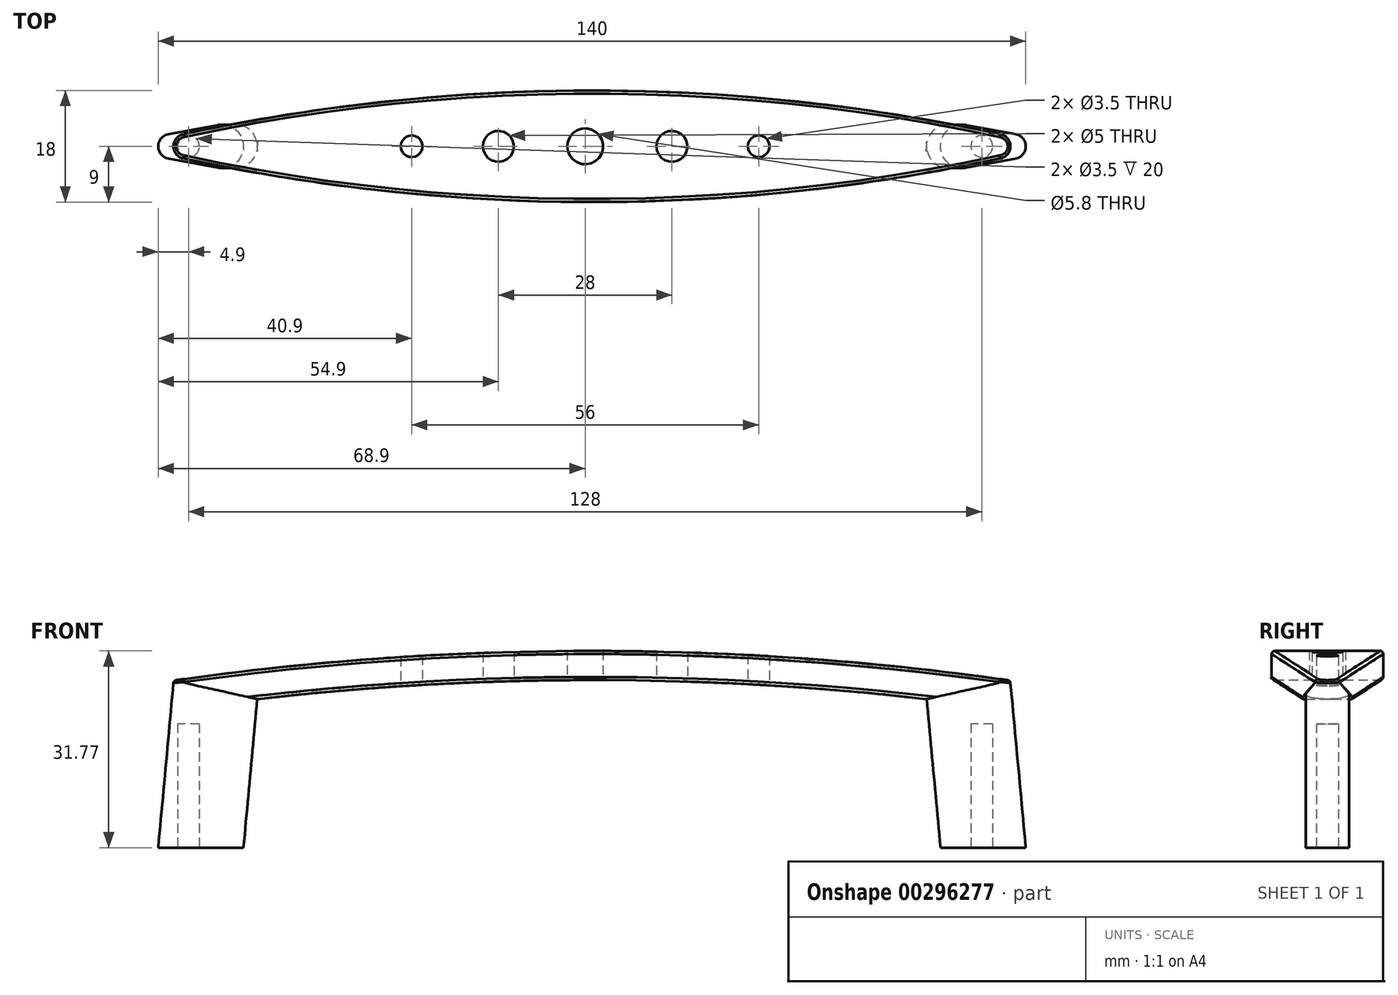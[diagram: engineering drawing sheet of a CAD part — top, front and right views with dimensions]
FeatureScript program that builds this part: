
annotation { "Feature Type Name" : "Feature", "Feature Type Description" : "" }
export const myFeature = defineFeature(function(context is Context, id is Id, definition is map)
    precondition{}
    {
        {
            var Q0;
            Q0=qCreatedBy(makeId("Front.planeOp"),FACE);
            var sketch = newSketch(context, id + "F0", { "sketchPlane" : qUnion([Q0])});
            skLineSegment(sketch, "E0", {"start": v(-66.42, 27) * mm, "end": v(68.58, 27) * mm, "construction": true});
            skLineSegment(sketch, "E1", {"start": v(-66.42, 27) * mm, "end": v(-68.9, 0) * mm});
            skLineSegment(sketch, "E2", {"start": v(68.58, 27) * mm, "end": v(71.1, 0) * mm});
            skLineSegment(sketch, "E3.0", {"start": v(-52.93, 24) * mm, "end": v(-55.14, 0) * mm});
            skLineSegment(sketch, "E4.0", {"start": v(55.1, 24) * mm, "end": v(57.34, 0) * mm});
            skLineSegment(sketch, "E5.0", {"start": v(-52.93, 24) * mm, "end": v(55.1, 24) * mm, "construction": true});
            skLineSegment(sketch, "E6", {"start": v(-68.9, 0) * mm, "end": v(-55.14, 0) * mm});
            skLineSegment(sketch, "E7", {"start": v(71.1, 0) * mm, "end": v(57.34, 0) * mm});
            skArc(sketch, "E8", {"start": v(68.58, 27) * mm, "mid": v(1.08, 31.77) * mm, "end": v(-66.42, 27) * mm});
            skArc(sketch, "E9", {"start": v(55.1, 24) * mm, "mid": v(1.09, 27.07) * mm, "end": v(-52.93, 24) * mm});
            skLineSegment(sketch, "E10", {"start": v(55.1, 24) * mm, "end": v(68.58, 27) * mm});
            skLineSegment(sketch, "E11", {"start": v(-52.93, 24) * mm, "end": v(-66.42, 27) * mm});
            skSolve(sketch);
        }
        {
            var Q0;
            Q0=qCreatedBy(makeId("Top.planeOp"),FACE);
            cPlane(context, id + "F1", {"entities" : qUnion([Q0]), "cplaneType" : CPlaneType.OFFSET, "offset" : 27 * mm, "width" : 150 * mm, "height" : 150 * mm});
        }
        {
            var Q0;
            Q0=qCreatedBy(id+"F1.planeOp",FACE);
            var sketch = newSketch(context, id + "F2", { "sketchPlane" : qUnion([Q0])});
            skCircle(sketch, "E12", {"center": v(66.58, 0) * mm, "radius": 2 * mm});
            skCircle(sketch, "E13", {"center": v(-64.42, 0) * mm, "radius": 2 * mm});
            skArc(sketch, "E14", {"start": v(-64.84, -1.95) * mm, "mid": v(1.08, -9) * mm, "end": v(67, -1.95) * mm});
            skArc(sketch, "E15", {"start": v(67, 1.95) * mm, "mid": v(1.08, 9) * mm, "end": v(-64.84, 1.95) * mm});
            skSolve(sketch);
        }
        {
            var Q0;
            Q0=qCreatedBy(makeId("Top.planeOp"),FACE);
            var sketch = newSketch(context, id + "F3", { "sketchPlane" : qUnion([Q0])});
            skArc(sketch, "E16", {"start": v(61.48, 3.44) * mm, "mid": v(57.34, 0) * mm, "end": v(61.48, -3.44) * mm});
            skArc(sketch, "E17", {"start": v(-59.27, -3.44) * mm, "mid": v(-55.14, 0) * mm, "end": v(-59.27, 3.44) * mm});
            skArc(sketch, "E18", {"start": v(69.47, -1.97) * mm, "mid": v(71.1, 0) * mm, "end": v(69.47, 1.97) * mm});
            skArc(sketch, "E19", {"start": v(-67.26, 1.97) * mm, "mid": v(-68.9, 0) * mm, "end": v(-67.26, -1.97) * mm});
            skLineSegment(sketch, "E20", {"start": v(69.47, -1.97) * mm, "end": v(61.48, -3.44) * mm});
            skLineSegment(sketch, "E21", {"start": v(69.47, 1.97) * mm, "end": v(61.48, 3.44) * mm});
            skLineSegment(sketch, "E22", {"start": v(-59.27, 3.44) * mm, "end": v(-67.26, 1.97) * mm});
            skLineSegment(sketch, "E23", {"start": v(-59.27, -3.44) * mm, "end": v(-67.26, -1.97) * mm});
            skSolve(sketch);
        }
        {
            var Q0;
            Q0=makeQuery(id+"F3.imprint","IMPRINT",FACE,{"disambiguationData":[TD([[makeQuery(id+"F3.imprint","IMPRINT",EDGE,{"derivedFrom":sQuery(id+"F3.wireOp",EDGE,"E16")}),1.0]])]});
            var Q1;
            Q1=sQuery(id+"F0.wireOp",EDGE,"E2");
            sweep(context, id + "F4", {"profiles" : qUnion([Q0]), "path" : qUnion([Q1])});
        }
        {
            var Q0;
            Q0=makeQuery(id+"F3.imprint","IMPRINT",FACE,{"disambiguationData":[TD([[makeQuery(id+"F3.imprint","IMPRINT",EDGE,{"derivedFrom":sQuery(id+"F3.wireOp",EDGE,"E17")}),1.0]])]});
            var Q1;
            Q1=sQuery(id+"F0.wireOp",EDGE,"E1");
            sweep(context, id + "F5", {"profiles" : qUnion([Q0]), "path" : qUnion([Q1])});
        }
        {
            var Q0;
            Q0=makeQuery(id+"F0.imprint","IMPRINT",FACE,{"disambiguationData":[TD([[makeQuery(id+"F0.imprint","IMPRINT",EDGE,{"derivedFrom":sQuery(id+"F0.wireOp",EDGE,"E8")}),1.0]])]});
            extrude(context, id + "F6", {"entities" : qUnion([Q0]), "endBound" : BoundingType.SYMMETRIC, "depth" : 18 * mm});
        }
        {
            var Q0;
            {var subQ0=sQuery(id+"F2.wireOp",EDGE,"E14");Q0=makeQuery(id+"F2.imprint","IMPRINT",FACE,{"disambiguationData":[TD([[makeQuery(id+"F2.imprint","IMPRINT",EDGE,{"derivedFrom":subQ0}),1.0]])]});}
            var Q1;
            {var subQ0=sQuery(id+"F2.wireOp",EDGE,"E12");var subQ1=makeQuery(id+"F2.imprint","INTERSECT",VERTEX,{"derivedFrom":[subQ0,sQuery(id+"F2.wireOp",EDGE,"E14")]});Q1=makeQuery(id+"F2.imprint","IMPRINT",FACE,{"disambiguationData":[TD([[makeQuery(id+"F2.imprint","IMPRINT",EDGE,{"disambiguationData":[TD([[subQ1,1.0]])],"derivedFrom":subQ0}),1.0]])]});}
            var Q2;
            {var subQ0=sQuery(id+"F2.wireOp",EDGE,"E13");var subQ1=makeQuery(id+"F2.imprint","INTERSECT",VERTEX,{"derivedFrom":[subQ0,sQuery(id+"F2.wireOp",EDGE,"E14")]});Q2=makeQuery(id+"F2.imprint","IMPRINT",FACE,{"disambiguationData":[TD([[makeQuery(id+"F2.imprint","IMPRINT",EDGE,{"disambiguationData":[TD([[subQ1,1.0]])],"derivedFrom":subQ0}),1.0]])]});}
            extrude(context, id + "F7", {"entities" : qUnion([Q0, Q1, Q2]), "endBound" : BoundingType.SYMMETRIC, "depth" : 25 * mm});
        }
        {
            var Q0;
            Q0=makeQuery(id+"F7.opExtrude","SWEPT_BODY",BODY,{"disambiguationData":[OSD([sQuery(id+"F2.wireOp",EDGE,"E12"),sQuery(id+"F2.wireOp",EDGE,"E13"),sQuery(id+"F2.wireOp",EDGE,"E14"),sQuery(id+"F2.wireOp",EDGE,"E15")])]});
            var Q1;
            Q1=makeQuery(id+"F6.opExtrude","SWEPT_BODY",BODY,{"disambiguationData":[OSD([sQuery(id+"F0.wireOp",EDGE,"E8"),sQuery(id+"F0.wireOp",EDGE,"E9"),sQuery(id+"F0.wireOp",EDGE,"E10"),sQuery(id+"F0.wireOp",EDGE,"E11")])]});
            booleanBodies(context, id + "F8", {"operationType" : BooleanOperationType.INTERSECTION, "tools" : qUnion([Q0, Q1])});
        }
        {
            var Q0;
            Q0=qCreatedBy(makeId("Top.planeOp"),FACE);
            var sketch = newSketch(context, id + "F9", { "sketchPlane" : qUnion([Q0])});
            skCircle(sketch, "E24", {"center": v(64, 0) * mm, "radius": 1.75 * mm});
            skCircle(sketch, "E25", {"center": v(-64, 0) * mm, "radius": 1.75 * mm});
            skSolve(sketch);
        }
        {
            var Q0;
            Q0=makeQuery(id+"F9.imprint","IMPRINT",FACE,{"disambiguationData":[TD([[makeQuery(id+"F9.imprint","IMPRINT",EDGE,{"derivedFrom":sQuery(id+"F9.wireOp",EDGE,"E24")}),1.0]])]});
            extrude(context, id + "F10", {"entities" : qUnion([Q0]), "operationType" : NewBodyOperationType.REMOVE, "depth" : 20 * mm});
        }
        {
            var Q0;
            Q0=makeQuery(id+"F9.imprint","IMPRINT",FACE,{"disambiguationData":[TD([[makeQuery(id+"F9.imprint","IMPRINT",EDGE,{"derivedFrom":sQuery(id+"F9.wireOp",EDGE,"E25")}),1.0]])]});
            extrude(context, id + "F11", {"entities" : qUnion([Q0]), "operationType" : NewBodyOperationType.REMOVE, "depth" : 20 * mm});
        }
        {
            var Q0;
            Q0=qCreatedBy(makeId("Top.planeOp"),FACE);
            var sketch = newSketch(context, id + "F12", { "sketchPlane" : qUnion([Q0])});
            skCircle(sketch, "E26", {"center": v(0, 0) * mm, "radius": 2.9 * mm});
            skCircle(sketch, "E27", {"center": v(14, 0) * mm, "radius": 2.5 * mm});
            skCircle(sketch, "E28", {"center": v(28, 0) * mm, "radius": 1.75 * mm});
            skCircle(sketch, "E29", {"center": v(-14, 0) * mm, "radius": 2.5 * mm});
            skCircle(sketch, "E30", {"center": v(-28, 0) * mm, "radius": 1.75 * mm});
            skSolve(sketch);
        }
        {
            var Q0;
            Q0=makeQuery(id+"F12.imprint","IMPRINT",FACE,{"disambiguationData":[TD([[makeQuery(id+"F12.imprint","IMPRINT",EDGE,{"derivedFrom":sQuery(id+"F12.wireOp",EDGE,"E30")}),1.0]])]});
            var Q1;
            Q1=makeQuery(id+"F12.imprint","IMPRINT",FACE,{"disambiguationData":[TD([[makeQuery(id+"F12.imprint","IMPRINT",EDGE,{"derivedFrom":sQuery(id+"F12.wireOp",EDGE,"E29")}),1.0]])]});
            var Q2;
            Q2=makeQuery(id+"F12.imprint","IMPRINT",FACE,{"disambiguationData":[TD([[makeQuery(id+"F12.imprint","IMPRINT",EDGE,{"derivedFrom":sQuery(id+"F12.wireOp",EDGE,"E26")}),1.0]])]});
            var Q3;
            Q3=makeQuery(id+"F12.imprint","IMPRINT",FACE,{"disambiguationData":[TD([[makeQuery(id+"F12.imprint","IMPRINT",EDGE,{"derivedFrom":sQuery(id+"F12.wireOp",EDGE,"E27")}),1.0]])]});
            var Q4;
            Q4=makeQuery(id+"F12.imprint","IMPRINT",FACE,{"disambiguationData":[TD([[makeQuery(id+"F12.imprint","IMPRINT",EDGE,{"derivedFrom":sQuery(id+"F12.wireOp",EDGE,"E28")}),1.0]])]});
            extrude(context, id + "F13", {"entities" : qUnion([Q0, Q1, Q2, Q3, Q4]), "operationType" : NewBodyOperationType.REMOVE, "endBound" : BoundingType.THROUGH_ALL, "depth" : 25 * mm});
        }
        {
            var Q0;
            Q0=makeQuery(id+"F8.opBoolean","INTERSECT",BODY,{"derivedFrom":[makeQuery(id+"F6.opExtrude","SWEPT_BODY",BODY,{"disambiguationData":[OSD([sQuery(id+"F0.wireOp",EDGE,"E8"),sQuery(id+"F0.wireOp",EDGE,"E9"),sQuery(id+"F0.wireOp",EDGE,"E10"),sQuery(id+"F0.wireOp",EDGE,"E11")])]}),makeQuery(id+"F7.opExtrude","SWEPT_BODY",BODY,{"disambiguationData":[OSD([sQuery(id+"F2.wireOp",EDGE,"E12"),sQuery(id+"F2.wireOp",EDGE,"E13"),sQuery(id+"F2.wireOp",EDGE,"E14"),sQuery(id+"F2.wireOp",EDGE,"E15")])]})]});
            var Q1;
            Q1=makeQuery(id+"F5.opSweep","SWEPT_BODY",BODY,{"disambiguationData":[OSD([sQuery(id+"F0.wireOp",EDGE,"E1"),sQuery(id+"F3.wireOp",EDGE,"E17"),sQuery(id+"F3.wireOp",EDGE,"E19"),sQuery(id+"F3.wireOp",EDGE,"E22"),sQuery(id+"F3.wireOp",EDGE,"E23")])]});
            var Q2;
            Q2=makeQuery(id+"F4.opSweep","SWEPT_BODY",BODY,{"disambiguationData":[OSD([sQuery(id+"F0.wireOp",EDGE,"E2"),sQuery(id+"F3.wireOp",EDGE,"E16"),sQuery(id+"F3.wireOp",EDGE,"E18"),sQuery(id+"F3.wireOp",EDGE,"E20"),sQuery(id+"F3.wireOp",EDGE,"E21")])]});
            booleanBodies(context, id + "F14", {"operationType" : BooleanOperationType.UNION, "tools" : qUnion([Q0, Q1, Q2])});
        }
        {
            var Q0;
            Q0=makeQuery(id+"F8.opBoolean","INTERSECT",EDGE,{"derivedFrom":[makeQuery(id+"F6.opExtrude","SWEPT_FACE",FACE,{"disambiguationData":[OSD([sQuery(id+"F0.wireOp",EDGE,"E8")])]}),makeQuery(id+"F7.opExtrude","SWEPT_FACE",FACE,{"disambiguationData":[OSD([sQuery(id+"F2.wireOp",EDGE,"E15")])]})]});
            var Q1;
            Q1=makeQuery(id+"F8.opBoolean","INTERSECT",EDGE,{"derivedFrom":[makeQuery(id+"F6.opExtrude","SWEPT_FACE",FACE,{"disambiguationData":[OSD([sQuery(id+"F0.wireOp",EDGE,"E9")])]}),makeQuery(id+"F7.opExtrude","SWEPT_FACE",FACE,{"disambiguationData":[OSD([sQuery(id+"F2.wireOp",EDGE,"E15")])]})]});
            var Q2;
            {var subQ0=sQuery(id+"F0.wireOp",EDGE,"E9");var subQ1=sQuery(id+"F0.wireOp",EDGE,"E10");Q2=makeQuery(id+"F14.opBoolean","SPLIT",EDGE,{"disambiguationData":[TD([makeQuery(id+"F7.opExtrude","SWEPT_FACE",FACE,{"disambiguationData":[OSD([sQuery(id+"F2.wireOp",EDGE,"E14")])]})])],"derivedFrom":makeQuery(id+"F6.opExtrude","SWEPT_EDGE",EDGE,{"disambiguationData":[OSD([sQuery(id+"F0.wireOp",EDGE,"E4.0"),subQ0,subQ1])]})});}
            var Q3;
            {var subQ0=sQuery(id+"F0.wireOp",EDGE,"E9");var subQ1=sQuery(id+"F0.wireOp",EDGE,"E10");Q3=makeQuery(id+"F14.opBoolean","SPLIT",EDGE,{"disambiguationData":[TD([makeQuery(id+"F7.opExtrude","SWEPT_FACE",FACE,{"disambiguationData":[OSD([sQuery(id+"F2.wireOp",EDGE,"E15")])]})])],"derivedFrom":makeQuery(id+"F6.opExtrude","SWEPT_EDGE",EDGE,{"disambiguationData":[OSD([sQuery(id+"F0.wireOp",EDGE,"E4.0"),subQ0,subQ1])]})});}
            var Q4;
            Q4=makeQuery(id+"F8.opBoolean","INTERSECT",EDGE,{"derivedFrom":[makeQuery(id+"F6.opExtrude","SWEPT_FACE",FACE,{"disambiguationData":[OSD([sQuery(id+"F0.wireOp",EDGE,"E9")])]}),makeQuery(id+"F7.opExtrude","SWEPT_FACE",FACE,{"disambiguationData":[OSD([sQuery(id+"F2.wireOp",EDGE,"E14")])]})]});
            var Q5;
            {var subQ0=sQuery(id+"F0.wireOp",EDGE,"E9");var subQ1=sQuery(id+"F0.wireOp",EDGE,"E11");Q5=makeQuery(id+"F14.opBoolean","SPLIT",EDGE,{"disambiguationData":[TD([makeQuery(id+"F7.opExtrude","SWEPT_FACE",FACE,{"disambiguationData":[OSD([sQuery(id+"F2.wireOp",EDGE,"E14")])]})])],"derivedFrom":makeQuery(id+"F6.opExtrude","SWEPT_EDGE",EDGE,{"disambiguationData":[OSD([sQuery(id+"F0.wireOp",EDGE,"E3.0"),subQ0,subQ1])]})});}
            var Q6;
            {var subQ0=sQuery(id+"F0.wireOp",EDGE,"E9");var subQ1=sQuery(id+"F0.wireOp",EDGE,"E11");Q6=makeQuery(id+"F14.opBoolean","SPLIT",EDGE,{"disambiguationData":[TD([makeQuery(id+"F7.opExtrude","SWEPT_FACE",FACE,{"disambiguationData":[OSD([sQuery(id+"F2.wireOp",EDGE,"E15")])]})])],"derivedFrom":makeQuery(id+"F6.opExtrude","SWEPT_EDGE",EDGE,{"disambiguationData":[OSD([sQuery(id+"F0.wireOp",EDGE,"E3.0"),subQ0,subQ1])]})});}
            fillet(context, id + "F15", {"entities" : qUnion([Q0, Q1, Q2, Q3, Q4, Q5, Q6]), "radius" : .5 * mm, "tangentPropagation" : true, "allowEdgeOverflow" : false});
        }
    });
